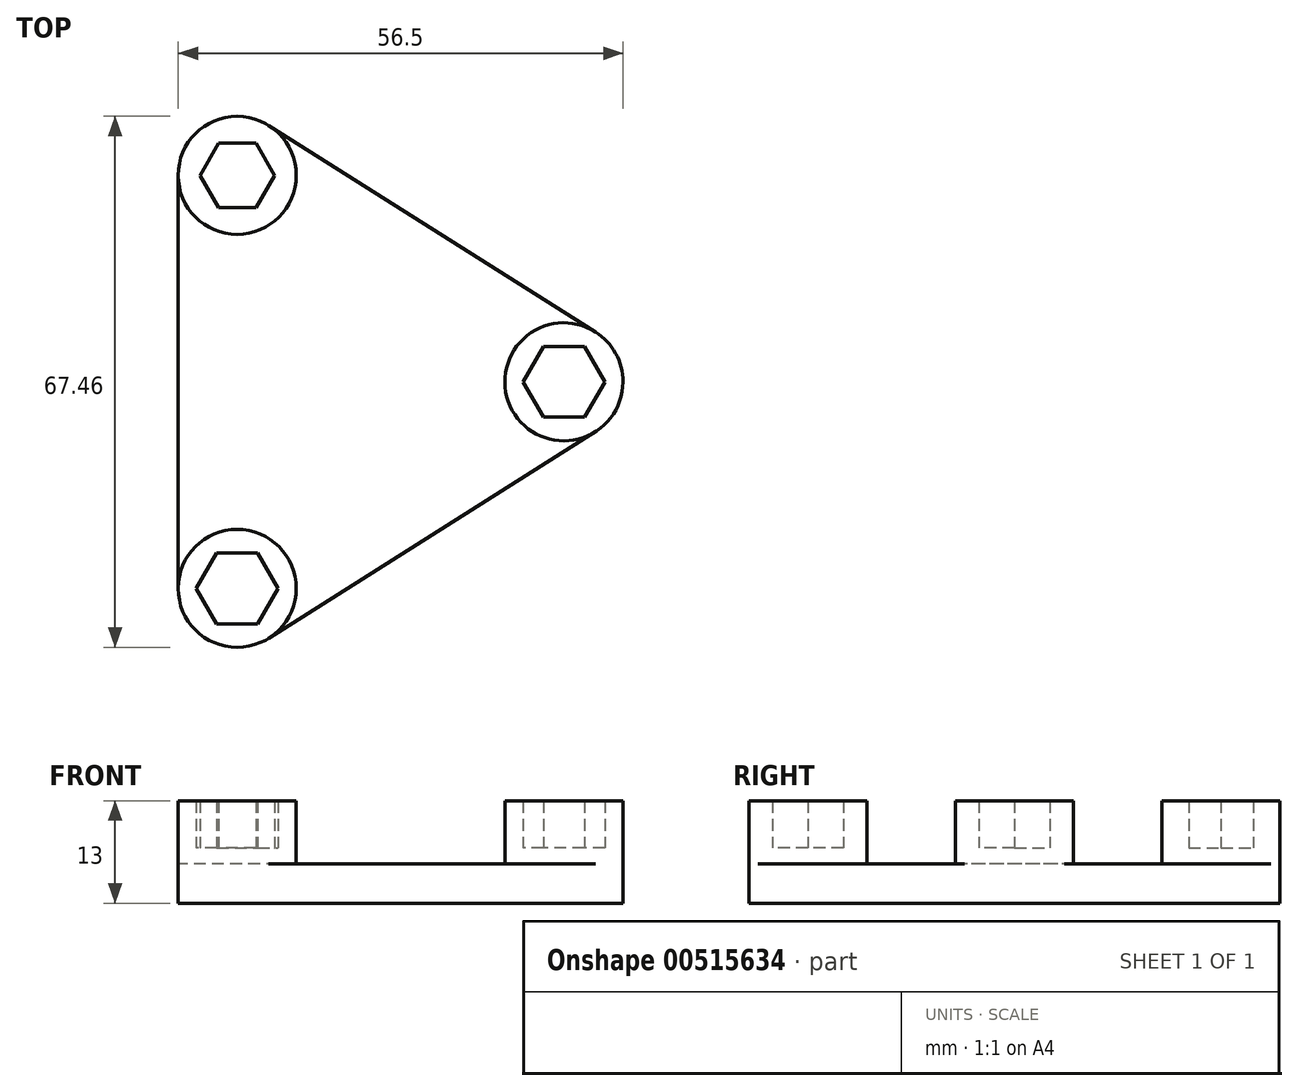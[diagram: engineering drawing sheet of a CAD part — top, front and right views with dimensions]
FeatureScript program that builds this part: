
annotation { "Feature Type Name" : "Feature", "Feature Type Description" : "" }
export const myFeature = defineFeature(function(context is Context, id is Id, definition is map)
    precondition{}
    {
        {
            var Q0;
            Q0=qCreatedBy(makeId("Top.planeOp"),FACE);
            var sketch = newSketch(context, id + "F0", { "sketchPlane" : qUnion([Q0])});
            skCircle(sketch, "E0", {"center": v(20.15, 0) * mm, "radius": 7.5 * mm});
            skCircle(sketch, "E1", {"center": v(-21.35, 26.23) * mm, "radius": 7.5 * mm});
            skCircle(sketch, "E2", {"center": v(-21.35, -26.23) * mm, "radius": 7.5 * mm});
            skLineSegment(sketch, "E3", {"start": v(-17.35, 32.57) * mm, "end": v(24.15, 6.34) * mm});
            skLineSegment(sketch, "E4", {"start": v(24.43, -6.16) * mm, "end": v(-17.35, -32.57) * mm});
            skLineSegment(sketch, "E5", {"start": v(-28.85, 26.23) * mm, "end": v(-28.85, -26.23) * mm});
            skCircle(sketch, "E6.cCircle", {"center": v(-21.35, -26.23) * mm, "radius": 4.5 * mm, "construction": true});
            skLineSegment(sketch, "E6.0", {"start": v(-18.76, -30.73) * mm, "end": v(-23.95, -30.73) * mm});
            skLineSegment(sketch, "E6.1", {"start": v(-23.95, -30.73) * mm, "end": v(-26.55, -26.23) * mm});
            skLineSegment(sketch, "E6.2", {"start": v(-26.55, -26.23) * mm, "end": v(-23.95, -21.73) * mm});
            skLineSegment(sketch, "E6.3", {"start": v(-23.95, -21.73) * mm, "end": v(-18.76, -21.73) * mm});
            skLineSegment(sketch, "E6.4", {"start": v(-18.76, -21.73) * mm, "end": v(-16.16, -26.23) * mm});
            skLineSegment(sketch, "E6.5", {"start": v(-16.16, -26.23) * mm, "end": v(-18.76, -30.73) * mm});
            skPoint(sketch, "E6.0.midPoint", {"position": v(-21.35, -30.73) * mm});
            skCircle(sketch, "E7.cCircle", {"center": v(-21.35, 26.23) * mm, "radius": 4.1 * mm, "construction": true});
            skLineSegment(sketch, "E7.0", {"start": v(-18.98, 22.13) * mm, "end": v(-23.72, 22.13) * mm});
            skLineSegment(sketch, "E7.1", {"start": v(-23.72, 22.13) * mm, "end": v(-26.1, 26.23) * mm});
            skLineSegment(sketch, "E7.2", {"start": v(-26.1, 26.23) * mm, "end": v(-23.72, 30.34) * mm});
            skLineSegment(sketch, "E7.3", {"start": v(-23.72, 30.34) * mm, "end": v(-18.98, 30.34) * mm});
            skLineSegment(sketch, "E7.4", {"start": v(-18.98, 30.34) * mm, "end": v(-16.61, 26.23) * mm});
            skLineSegment(sketch, "E7.5", {"start": v(-16.61, 26.23) * mm, "end": v(-18.98, 22.13) * mm});
            skPoint(sketch, "E7.0.midPoint", {"position": v(-21.35, 22.13) * mm});
            skLineSegment(sketch, "E8", {"start": v(-21.35, 26.23) * mm, "end": v(-21.35, -26.23) * mm});
            skCircle(sketch, "E9.cCircle", {"center": v(20.15, 0) * mm, "radius": 4.5 * mm, "construction": true});
            skLineSegment(sketch, "E9.0", {"start": v(22.74, -4.5) * mm, "end": v(17.55, -4.5) * mm});
            skLineSegment(sketch, "E9.1", {"start": v(17.55, -4.5) * mm, "end": v(14.95, 0) * mm});
            skLineSegment(sketch, "E9.2", {"start": v(14.95, 0) * mm, "end": v(17.55, 4.5) * mm});
            skLineSegment(sketch, "E9.3", {"start": v(17.55, 4.5) * mm, "end": v(22.74, 4.5) * mm});
            skLineSegment(sketch, "E9.4", {"start": v(22.74, 4.5) * mm, "end": v(25.34, 0) * mm});
            skLineSegment(sketch, "E9.5", {"start": v(25.34, 0) * mm, "end": v(22.74, -4.5) * mm});
            skPoint(sketch, "E9.0.midPoint", {"position": v(20.15, -4.5) * mm});
            skSolve(sketch);
        }
        {
            var Q0;
            {var subQ0=sQuery(id+"F0.wireOp",EDGE,"E5");Q0=makeQuery(id+"F0.imprint","IMPRINT",FACE,{"disambiguationData":[TD([[makeQuery(id+"F0.imprint","IMPRINT",EDGE,{"derivedFrom":subQ0}),1.0]])]});}
            var Q1;
            {var subQ0=sQuery(id+"F0.wireOp",EDGE,"E3");Q1=makeQuery(id+"F0.imprint","IMPRINT",FACE,{"disambiguationData":[TD([[makeQuery(id+"F0.imprint","IMPRINT",EDGE,{"derivedFrom":subQ0}),-1.0]])]});}
            extrude(context, id + "F1", {"entities" : qUnion([Q0, Q1]), "depth" : 5 * mm, "offsetDistance" : 25 * mm});
        }
        {
            var Q0;
            Q0=makeQuery(id+"F0.imprint","IMPRINT",FACE,{"disambiguationData":[TD([[makeQuery(id+"F0.imprint","IMPRINT",EDGE,{"derivedFrom":sQuery(id+"F0.wireOp",EDGE,"E6.0")}),1.0]])]});
            var Q1;
            Q1=makeQuery(id+"F0.imprint","IMPRINT",FACE,{"disambiguationData":[TD([[makeQuery(id+"F0.imprint","IMPRINT",EDGE,{"derivedFrom":sQuery(id+"F0.wireOp",EDGE,"E9.0")}),1.0]])]});
            var Q2;
            {var subQ7=sQuery(id+"F0.wireOp",EDGE,"E7.1");Q2=makeQuery(id+"F0.imprint","IMPRINT",FACE,{"disambiguationData":[TD([[makeQuery(id+"F0.imprint","IMPRINT",EDGE,{"derivedFrom":subQ7}),1.0]])]});}
            extrude(context, id + "F2", {"entities" : qUnion([Q0, Q1, Q2]), "operationType" : NewBodyOperationType.ADD, "depth" : 13 * mm, "offsetDistance" : 25 * mm});
        }
        {
            var Q0;
            {var subQ0=sQuery(id+"F0.wireOp",EDGE,"E7.1");Q0=makeQuery(id+"F0.imprint","IMPRINT",FACE,{"disambiguationData":[TD([[makeQuery(id+"F0.imprint","IMPRINT",EDGE,{"derivedFrom":subQ0}),-1.0]])]});}
            var Q1;
            Q1=makeQuery(id+"F0.imprint","IMPRINT",FACE,{"disambiguationData":[TD([[makeQuery(id+"F0.imprint","IMPRINT",EDGE,{"derivedFrom":sQuery(id+"F0.wireOp",EDGE,"E6.0")}),-1.0]])]});
            var Q2;
            Q2=makeQuery(id+"F0.imprint","IMPRINT",FACE,{"disambiguationData":[TD([[makeQuery(id+"F0.imprint","IMPRINT",EDGE,{"derivedFrom":sQuery(id+"F0.wireOp",EDGE,"E9.0")}),-1.0]])]});
            extrude(context, id + "F3", {"entities" : qUnion([Q0, Q1, Q2]), "operationType" : NewBodyOperationType.ADD, "depth" : 7 * mm, "offsetDistance" : 25 * mm});
        }
    });
